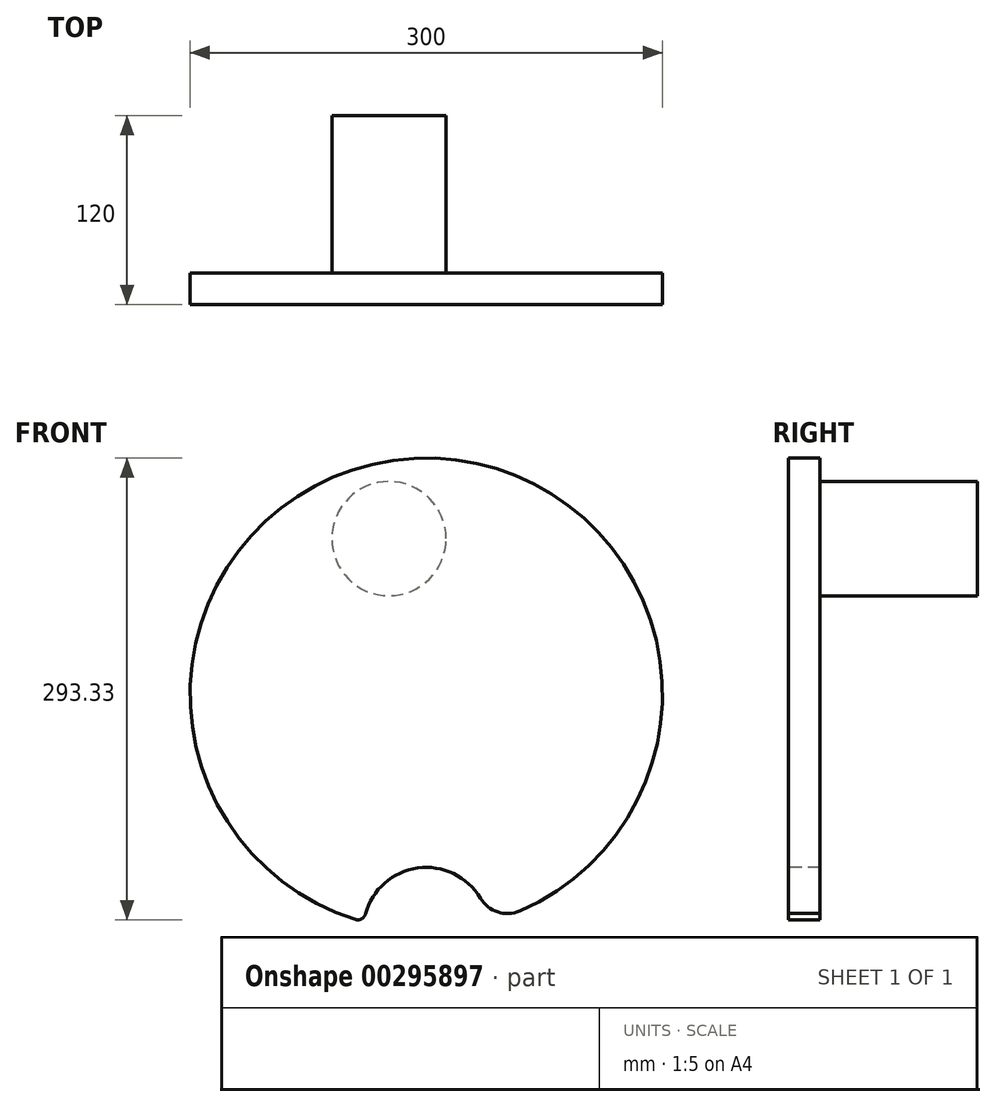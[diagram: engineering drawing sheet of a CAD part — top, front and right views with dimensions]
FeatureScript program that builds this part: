
annotation { "Feature Type Name" : "Feature", "Feature Type Description" : "" }
export const myFeature = defineFeature(function(context is Context, id is Id, definition is map)
    precondition{}
    {
        {
            var Q0;
            Q0=qCreatedBy(makeId("Front.planeOp"),FACE);
            var sketch = newSketch(context, id + "F0", { "sketchPlane" : qUnion([Q0])});
            skCircle(sketch, "E0", {"center": v(0, 0) * mm, "radius": 150 * mm});
            skSolve(sketch);
        }
        {
            var Q0;
            Q0=makeQuery(id+"F0.imprint","IMPRINT",FACE,{"disambiguationData":[TD([[makeQuery(id+"F0.imprint","IMPRINT",EDGE,{"derivedFrom":sQuery(id+"F0.wireOp",EDGE,"E0")}),1.0]])]});
            extrude(context, id + "F1", {"entities" : qUnion([Q0]), "depth" : 20 * mm});
        }
        {
            var Q0;
            Q0=makeQuery(id+"F1.opExtrude","CAP_FACE",FACE,{"disambiguationData":[OSD([sQuery(id+"F0.wireOp",EDGE,"E0")])],"isStart":false});
            var sketch = newSketch(context, id + "F2", { "sketchPlane" : qUnion([Q0])});
            skCircle(sketch, "E1", {"center": v(0, -150) * mm, "radius": 40 * mm});
            skSolve(sketch);
        }
        {
            var Q0;
            Q0 = qSketchRegion(id + "F2", true);
            extrude(context, id + "F3", {"entities" : qUnion([Q0]), "operationType" : NewBodyOperationType.REMOVE, "oppositeDirection" : true, "depth" : 25 * mm});
        }
        {
            var Q0;
            Q0=makeQuery(id+"F3.boolean.opBoolean","INTERSECT",EDGE,{"disambiguationData":[OD(0.0)],"derivedFrom":[makeQuery(id+"F1.opExtrude","SWEPT_FACE",FACE,{"disambiguationData":[OSD([sQuery(id+"F0.wireOp",EDGE,"E0")])]}),makeQuery(id+"F3.opExtrude","SWEPT_FACE",FACE,{"disambiguationData":[OSD([sQuery(id+"F2.wireOp",EDGE,"E1")])]})]});
            fillet(context, id + "F4", {"entities" : qUnion([Q0]), "radius" : 5 * mm, "tangentPropagation" : true, "allowEdgeOverflow" : false});
        }
        {
            var Q0;
            Q0=makeQuery(id+"F3.boolean.opBoolean","INTERSECT",EDGE,{"disambiguationData":[OD(1.0)],"derivedFrom":[makeQuery(id+"F1.opExtrude","SWEPT_FACE",FACE,{"disambiguationData":[OSD([sQuery(id+"F0.wireOp",EDGE,"E0")])]}),makeQuery(id+"F3.opExtrude","SWEPT_FACE",FACE,{"disambiguationData":[OSD([sQuery(id+"F2.wireOp",EDGE,"E1")])]})]});
            fillet(context, id + "F5", {"entities" : qUnion([Q0]), "radius" : 20 * mm, "tangentPropagation" : true, "allowEdgeOverflow" : false});
        }
        {
            var Q0;
            Q0=makeQuery(id+"F1.opExtrude","CAP_FACE",FACE,{"disambiguationData":[OSD([sQuery(id+"F0.wireOp",EDGE,"E0")])],"isStart":true});
            var sketch = newSketch(context, id + "F6", { "sketchPlane" : qUnion([Q0])});
            skCircle(sketch, "E2", {"center": v(23.68, 98.81) * mm, "radius": 36.27 * mm});
            skSolve(sketch);
        }
        {
            var Q0;
            Q0=makeQuery(id+"F6.imprint","IMPRINT",FACE,{"disambiguationData":[TD([[makeQuery(id+"F6.imprint","IMPRINT",EDGE,{"derivedFrom":sQuery(id+"F6.wireOp",EDGE,"E2")}),1.0]])]});
            var Q1;
            Q1=sQuery(id+"F6.wireOp",EDGE,"E2");
            extrude(context, id + "F7", {"entities" : qUnion([Q0]), "operationType" : NewBodyOperationType.ADD, "surfaceEntities" : qUnion([Q1]), "depth" : 100 * mm, "offsetDistance" : 25 * mm});
        }
    });
